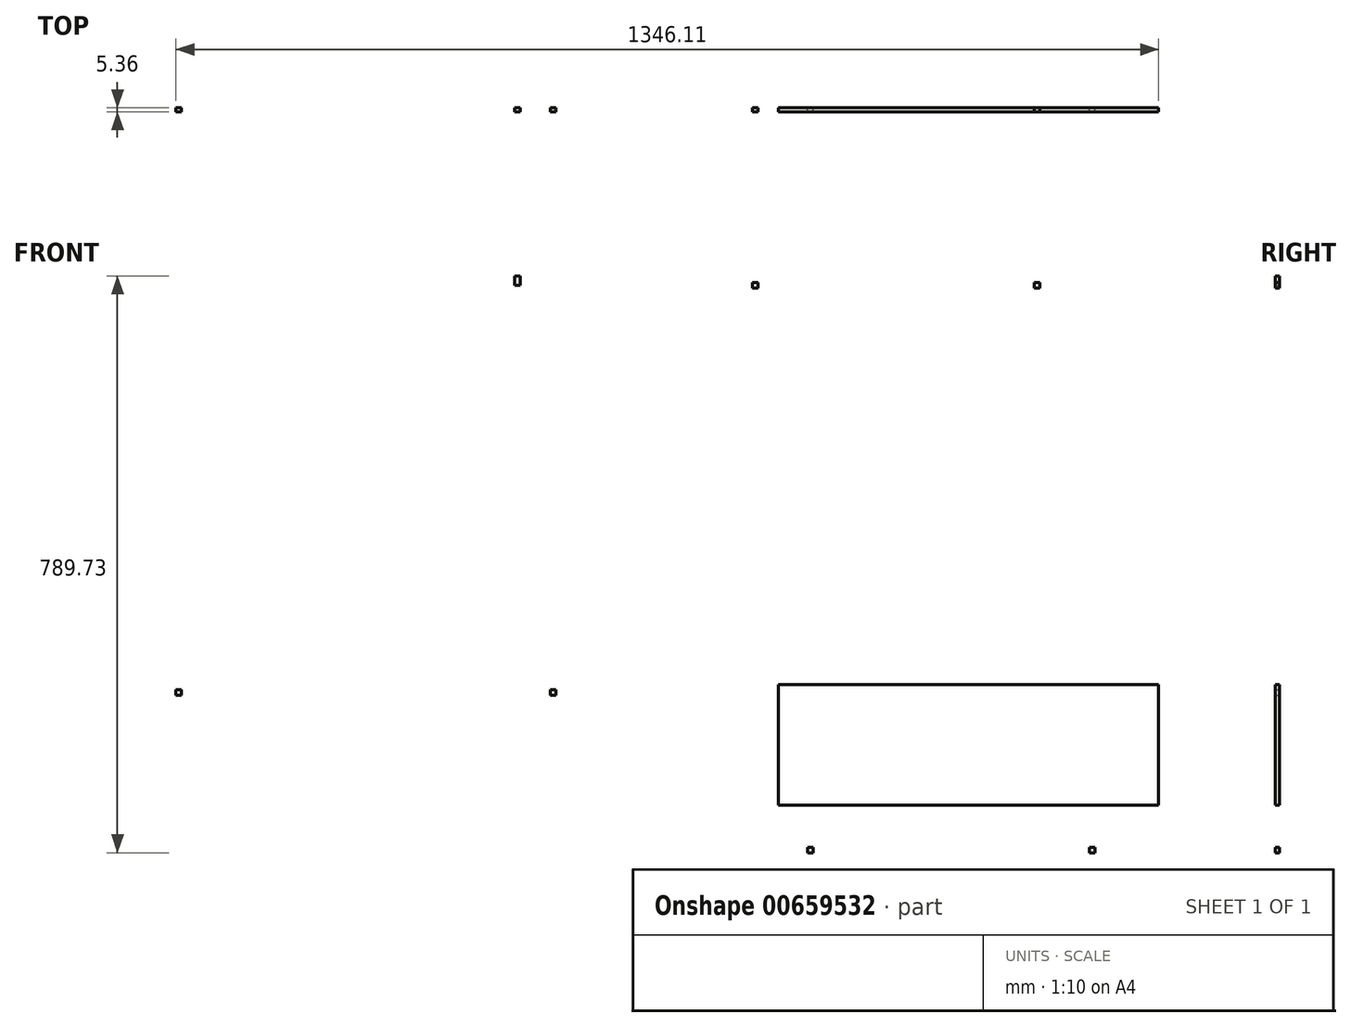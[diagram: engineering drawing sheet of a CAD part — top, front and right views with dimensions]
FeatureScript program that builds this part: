
annotation { "Feature Type Name" : "Feature", "Feature Type Description" : "" }
export const myFeature = defineFeature(function(context is Context, id is Id, definition is map)
    precondition{}
    {
        {
            var Q0;
            Q0=qCreatedBy(makeId("Front.planeOp"),FACE);
            var sketch = newSketch(context, id + "F0", { "sketchPlane" : qUnion([Q0])});
            skLineSegment(sketch, "E0.bottom", {"start": v(-383.36, 350.1) * mm, "end": v(61.14, 350.1) * mm});
            skLineSegment(sketch, "E0.top", {"start": v(-383.36, -43.6) * mm, "end": v(61.14, -43.6) * mm});
            skLineSegment(sketch, "E0.left", {"start": v(-383.36, 350.1) * mm, "end": v(-383.36, -43.6) * mm});
            skLineSegment(sketch, "E0.right", {"start": v(61.14, 350.1) * mm, "end": v(61.14, -43.6) * mm});
            skLineSegment(sketch, "E1.bottom", {"start": v(61.14, -43.6) * mm, "end": v(53.52, -43.6) * mm});
            skLineSegment(sketch, "E1.top", {"start": v(61.14, -30.9) * mm, "end": v(53.52, -30.9) * mm});
            skLineSegment(sketch, "E1.left", {"start": v(61.14, -43.6) * mm, "end": v(61.14, -30.9) * mm});
            skLineSegment(sketch, "E1.right", {"start": v(53.52, -43.6) * mm, "end": v(53.52, -30.9) * mm});
            skLineSegment(sketch, "E2.bottom", {"start": v(61.14, 350.1) * mm, "end": v(53.52, 350.1) * mm});
            skLineSegment(sketch, "E2.top", {"start": v(61.14, 337.4) * mm, "end": v(53.52, 337.4) * mm});
            skLineSegment(sketch, "E2.left", {"start": v(61.14, 350.1) * mm, "end": v(61.14, 337.4) * mm});
            skLineSegment(sketch, "E2.right", {"start": v(53.52, 350.1) * mm, "end": v(53.52, 337.4) * mm});
            skSolve(sketch);
        }
        {
            var Q0;
            Q0=makeQuery(id+"F0.imprint","IMPRINT",FACE,{"disambiguationData":[TD([[makeQuery(id+"F0.imprint","IMPRINT",EDGE,{"derivedFrom":sQuery(id+"F0.wireOp",EDGE,"E0.bottom")}),-1.0]])]});
            extrude(context, id + "F1", {"entities" : qUnion([Q0]), "depth" : 5.36 * mm, "offsetDistance" : 25.4 * mm});
        }
        {
            var Q0;
            Q0=qCreatedBy(makeId("Front.planeOp"),FACE);
            var sketch = newSketch(context, id + "F2", { "sketchPlane" : qUnion([Q0])});
            skLineSegment(sketch, "E3.bottom", {"start": v(379.41, 341.51) * mm, "end": v(773.11, 341.51) * mm});
            skLineSegment(sketch, "E3.top", {"start": v(379.41, -52.19) * mm, "end": v(773.11, -52.19) * mm});
            skLineSegment(sketch, "E3.left", {"start": v(379.41, 341.51) * mm, "end": v(379.41, -52.19) * mm});
            skLineSegment(sketch, "E3.right", {"start": v(773.11, 341.51) * mm, "end": v(773.11, -52.19) * mm});
            skLineSegment(sketch, "E4.bottom", {"start": v(379.41, 341.51) * mm, "end": v(387.03, 341.51) * mm});
            skLineSegment(sketch, "E4.top", {"start": v(379.41, 333.9) * mm, "end": v(387.03, 333.9) * mm});
            skLineSegment(sketch, "E4.left", {"start": v(379.41, 341.51) * mm, "end": v(379.41, 333.9) * mm});
            skLineSegment(sketch, "E4.right", {"start": v(387.03, 341.51) * mm, "end": v(387.03, 333.9) * mm});
            skLineSegment(sketch, "E5.bottom", {"start": v(379.41, -52.19) * mm, "end": v(387.03, -52.19) * mm});
            skLineSegment(sketch, "E5.top", {"start": v(379.41, -44.57) * mm, "end": v(387.03, -44.57) * mm});
            skLineSegment(sketch, "E5.left", {"start": v(379.41, -52.19) * mm, "end": v(379.41, -44.57) * mm});
            skLineSegment(sketch, "E5.right", {"start": v(387.03, -52.19) * mm, "end": v(387.03, -44.57) * mm});
            skLineSegment(sketch, "E6.bottom", {"start": v(773.11, -52.19) * mm, "end": v(765.5, -52.19) * mm});
            skLineSegment(sketch, "E6.top", {"start": v(773.11, -44.57) * mm, "end": v(765.5, -44.57) * mm});
            skLineSegment(sketch, "E6.left", {"start": v(773.11, -52.19) * mm, "end": v(773.11, -44.57) * mm});
            skLineSegment(sketch, "E6.right", {"start": v(765.5, -52.19) * mm, "end": v(765.5, -44.57) * mm});
            skLineSegment(sketch, "E7.bottom", {"start": v(773.11, 341.51) * mm, "end": v(765.5, 341.51) * mm});
            skLineSegment(sketch, "E7.top", {"start": v(773.11, 333.9) * mm, "end": v(765.5, 333.9) * mm});
            skLineSegment(sketch, "E7.left", {"start": v(773.11, 341.51) * mm, "end": v(773.11, 333.9) * mm});
            skLineSegment(sketch, "E7.right", {"start": v(765.5, 341.51) * mm, "end": v(765.5, 333.9) * mm});
            skSolve(sketch);
        }
        {
            var Q0;
            Q0=makeQuery(id+"F2.imprint","IMPRINT",FACE,{"disambiguationData":[TD([[makeQuery(id+"F2.imprint","IMPRINT",EDGE,{"derivedFrom":sQuery(id+"F2.wireOp",EDGE,"E3.bottom")}),-1.0]])]});
            extrude(context, id + "F3", {"entities" : qUnion([Q0]), "depth" : 5.36 * mm, "offsetDistance" : 25.4 * mm});
        }
        {
            var Q0;
            Q0=qCreatedBy(makeId("Front.planeOp"),FACE);
            var sketch = newSketch(context, id + "F4", { "sketchPlane" : qUnion([Q0])});
            skLineSegment(sketch, "E8.bottom", {"start": v(-410.37, -216.38) * mm, "end": v(110.33, -216.38) * mm});
            skLineSegment(sketch, "E8.top", {"start": v(-410.37, -610.08) * mm, "end": v(110.33, -610.08) * mm});
            skLineSegment(sketch, "E8.left", {"start": v(-410.37, -216.38) * mm, "end": v(-410.37, -610.08) * mm});
            skLineSegment(sketch, "E8.right", {"start": v(110.33, -216.38) * mm, "end": v(110.33, -610.08) * mm});
            skLineSegment(sketch, "E9.bottom", {"start": v(-410.37, -216.38) * mm, "end": v(-402.75, -216.38) * mm});
            skLineSegment(sketch, "E9.top", {"start": v(-410.37, -224) * mm, "end": v(-402.75, -224) * mm});
            skLineSegment(sketch, "E9.left", {"start": v(-410.37, -216.38) * mm, "end": v(-410.37, -224) * mm});
            skLineSegment(sketch, "E9.right", {"start": v(-402.75, -216.38) * mm, "end": v(-402.75, -224) * mm});
            skLineSegment(sketch, "E10.bottom", {"start": v(-410.37, -610.08) * mm, "end": v(-402.75, -610.08) * mm});
            skLineSegment(sketch, "E10.top", {"start": v(-410.37, -602.46) * mm, "end": v(-402.75, -602.46) * mm});
            skLineSegment(sketch, "E10.left", {"start": v(-410.37, -610.08) * mm, "end": v(-410.37, -602.46) * mm});
            skLineSegment(sketch, "E10.right", {"start": v(-402.75, -610.08) * mm, "end": v(-402.75, -602.46) * mm});
            skLineSegment(sketch, "E11.bottom", {"start": v(110.33, -610.08) * mm, "end": v(102.71, -610.08) * mm});
            skLineSegment(sketch, "E11.top", {"start": v(110.33, -602.46) * mm, "end": v(102.71, -602.46) * mm});
            skLineSegment(sketch, "E11.left", {"start": v(110.33, -610.08) * mm, "end": v(110.33, -602.46) * mm});
            skLineSegment(sketch, "E11.right", {"start": v(102.71, -610.08) * mm, "end": v(102.71, -602.46) * mm});
            skLineSegment(sketch, "E12.bottom", {"start": v(110.33, -216.38) * mm, "end": v(102.71, -216.38) * mm});
            skLineSegment(sketch, "E12.top", {"start": v(110.33, -224) * mm, "end": v(102.71, -224) * mm});
            skLineSegment(sketch, "E12.left", {"start": v(110.33, -216.38) * mm, "end": v(110.33, -224) * mm});
            skLineSegment(sketch, "E12.right", {"start": v(102.71, -216.38) * mm, "end": v(102.71, -224) * mm});
            skSolve(sketch);
        }
        {
            var Q0;
            Q0=makeQuery(id+"F4.imprint","IMPRINT",FACE,{"disambiguationData":[TD([[makeQuery(id+"F4.imprint","IMPRINT",EDGE,{"derivedFrom":sQuery(id+"F4.wireOp",EDGE,"E8.bottom")}),-1.0]])]});
            var Q1;
            Q1=makeQuery(id+"F4.imprint","IMPRINT",FACE,{"disambiguationData":[TD([[makeQuery(id+"F4.imprint","IMPRINT",EDGE,{"derivedFrom":sQuery(id+"F4.wireOp",EDGE,"E9.bottom")}),-1.0]])]});
            var Q2;
            Q2=makeQuery(id+"F4.imprint","IMPRINT",FACE,{"disambiguationData":[TD([[makeQuery(id+"F4.imprint","IMPRINT",EDGE,{"derivedFrom":sQuery(id+"F4.wireOp",EDGE,"E10.bottom")}),1.0]])]});
            var Q3;
            Q3=makeQuery(id+"F4.imprint","IMPRINT",FACE,{"disambiguationData":[TD([[makeQuery(id+"F4.imprint","IMPRINT",EDGE,{"derivedFrom":sQuery(id+"F4.wireOp",EDGE,"E11.bottom")}),-1.0]])]});
            var Q4;
            Q4=makeQuery(id+"F4.imprint","IMPRINT",FACE,{"disambiguationData":[TD([[makeQuery(id+"F4.imprint","IMPRINT",EDGE,{"derivedFrom":sQuery(id+"F4.wireOp",EDGE,"E12.bottom")}),1.0]])]});
            extrude(context, id + "F5", {"entities" : qUnion([Q0, Q1, Q2, Q3, Q4]), "depth" : 5.36 * mm, "offsetDistance" : 25.4 * mm});
        }
        {
            var Q0;
            Q0=qCreatedBy(makeId("Front.planeOp"),FACE);
            var sketch = newSketch(context, id + "F6", { "sketchPlane" : qUnion([Q0])});
            skLineSegment(sketch, "E13.bottom", {"start": v(455.12, -432.01) * mm, "end": v(848.82, -432.01) * mm});
            skLineSegment(sketch, "E13.top", {"start": v(455.12, -597.11) * mm, "end": v(848.82, -597.11) * mm});
            skLineSegment(sketch, "E13.left", {"start": v(455.12, -432.01) * mm, "end": v(455.12, -597.11) * mm});
            skLineSegment(sketch, "E13.right", {"start": v(848.82, -432.01) * mm, "end": v(848.82, -597.11) * mm});
            skLineSegment(sketch, "E14.bottom", {"start": v(455.12, -432.01) * mm, "end": v(462.74, -432.01) * mm});
            skLineSegment(sketch, "E14.top", {"start": v(455.12, -439.63) * mm, "end": v(462.74, -439.63) * mm});
            skLineSegment(sketch, "E14.left", {"start": v(455.12, -432.01) * mm, "end": v(455.12, -439.63) * mm});
            skLineSegment(sketch, "E14.right", {"start": v(462.74, -432.01) * mm, "end": v(462.74, -439.63) * mm});
            skLineSegment(sketch, "E15.bottom", {"start": v(455.12, -597.11) * mm, "end": v(462.74, -597.11) * mm});
            skLineSegment(sketch, "E15.top", {"start": v(455.12, -589.5) * mm, "end": v(462.74, -589.5) * mm});
            skLineSegment(sketch, "E15.left", {"start": v(455.12, -597.11) * mm, "end": v(455.12, -589.5) * mm});
            skLineSegment(sketch, "E15.right", {"start": v(462.74, -597.11) * mm, "end": v(462.74, -589.5) * mm});
            skLineSegment(sketch, "E16.bottom", {"start": v(848.82, -432.01) * mm, "end": v(841.2, -432.01) * mm});
            skLineSegment(sketch, "E16.top", {"start": v(848.82, -439.63) * mm, "end": v(841.2, -439.63) * mm});
            skLineSegment(sketch, "E16.left", {"start": v(848.82, -432.01) * mm, "end": v(848.82, -439.63) * mm});
            skLineSegment(sketch, "E16.right", {"start": v(841.2, -432.01) * mm, "end": v(841.2, -439.63) * mm});
            skLineSegment(sketch, "E17.bottom", {"start": v(848.82, -597.11) * mm, "end": v(841.2, -597.11) * mm});
            skLineSegment(sketch, "E17.top", {"start": v(848.82, -589.5) * mm, "end": v(841.2, -589.5) * mm});
            skLineSegment(sketch, "E17.left", {"start": v(848.82, -597.11) * mm, "end": v(848.82, -589.5) * mm});
            skLineSegment(sketch, "E17.right", {"start": v(841.2, -597.11) * mm, "end": v(841.2, -589.5) * mm});
            skSolve(sketch);
        }
        {
            var Q0;
            Q0=makeQuery(id+"F6.imprint","IMPRINT",FACE,{"disambiguationData":[TD([[makeQuery(id+"F6.imprint","IMPRINT",EDGE,{"derivedFrom":sQuery(id+"F6.wireOp",EDGE,"E13.bottom")}),-1.0]])]});
            extrude(context, id + "F7", {"entities" : qUnion([Q0]), "depth" : 5.36 * mm, "offsetDistance" : 25.4 * mm});
        }
        {
            var Q0;
            Q0=qCreatedBy(makeId("Front.planeOp"),FACE);
            var sketch = newSketch(context, id + "F8", { "sketchPlane" : qUnion([Q0])});
            skLineSegment(sketch, "E18.bottom", {"start": v(415.04, -209.07) * mm, "end": v(935.74, -209.07) * mm});
            skLineSegment(sketch, "E18.top", {"start": v(415.04, -374.17) * mm, "end": v(935.74, -374.17) * mm});
            skLineSegment(sketch, "E18.left", {"start": v(415.04, -209.07) * mm, "end": v(415.04, -374.17) * mm});
            skLineSegment(sketch, "E18.right", {"start": v(935.74, -209.07) * mm, "end": v(935.74, -374.17) * mm});
            skSolve(sketch);
        }
        {
            var Q0;
            Q0=makeQuery(id+"F8.imprint","IMPRINT",FACE,{"disambiguationData":[TD([[makeQuery(id+"F8.imprint","IMPRINT",EDGE,{"derivedFrom":sQuery(id+"F8.wireOp",EDGE,"E18.bottom")}),-1.0]])]});
            extrude(context, id + "F9", {"entities" : qUnion([Q0]), "depth" : 5.36 * mm, "offsetDistance" : 25.4 * mm});
        }
    });
